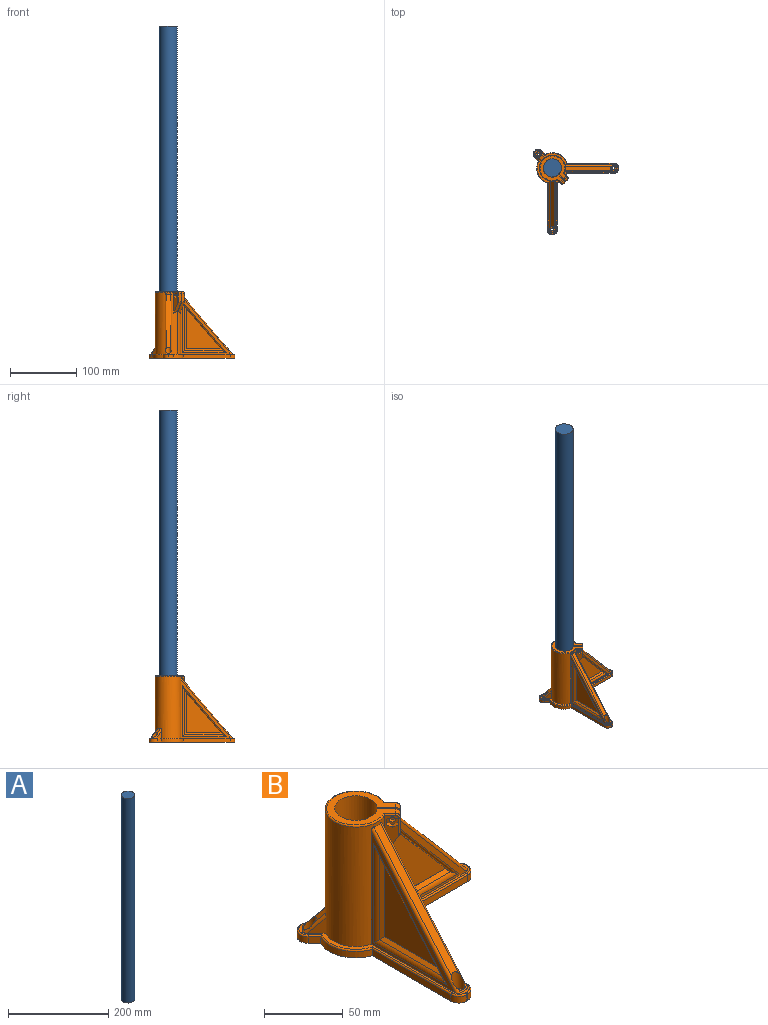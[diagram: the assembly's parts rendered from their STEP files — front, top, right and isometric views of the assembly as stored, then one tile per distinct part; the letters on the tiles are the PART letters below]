
ASSEMBLY  parts=2 mates=1
PART A: 3 faces, bbox 27x27x500 mm
  f0: cylinder r=13.5mm len=500mm, axis (0,0,-1), area 42411.5mm2, adj f1,f2
  f1: plane 27x27mm, normal (0,0,1), area 572.6mm2, adj f0
  f2: plane 27x27mm, normal (0,0,-1), area 572.6mm2, adj f0
PART B: 132 faces, bbox 129.9x129.9x100.3 mm
  f0: plane 5.4x5.4mm, normal (-0.5,0.5,0.71), area 6.3mm2, adj f9,f53,f122,f123
  f1: plane 6x2.19mm, normal (0.76,0,0.65), area 9.1mm2, adj f9,f56,f81,f82
  f2: plane 6x2.19mm, normal (0,-0.76,0.65), area 9.1mm2, adj f9,f50,f79,f80
  f3: plane 87.84x75.23mm, normal (0,-1,0), area 745.8mm2, adj f8,f9,f82,f118,f126,f127
  f4: plane 87.84x75.23mm, normal (0,1,0), area 745.8mm2, adj f8,f9,f81,f119,f130,f131
  f5: plane 87.84x75.23mm, normal (-1,0,0), area 745.8mm2, adj f8,f9,f80,f121,f124,f125
  f6: plane 31.32x6.36mm, normal (-0.71,-0.71,0), area 162.2mm2, adj f8,f34,f41,f42,f43,f44,f45,f46
  f7: cylinder r=2.2mm len=5.23mm, axis (0.71,0.71,0), area 41.5mm2, adj f25,f47
  f8: cylinder r=19.5mm len=93mm, axis (0,0,-1), area 8919.4mm2, adj f3,f4,f5,f6,f9,f24,f25,f27
  f9: plane 126.76x126.76mm, normal (0,0,1), area 852.8mm2, adj f0,f1,f2,f3,f4,f5,f8,f21
  f10: plane 70.73x5mm, normal (1,0,0), area 353.6mm2, adj f11,f23,f74,f96
  f11: cylinder r=23.5mm len=14.77mm, axis (0,0,-1), area 108.2mm2, adj f10,f12,f23,f94
  f12: plane 70.73x5mm, normal (0,-1,0), area 353.6mm2, adj f11,f23,f75,f92
  f13: plane 5x1mm, normal (1,0,0), area 5mm2, adj f23,f75,f76,f93
  f14: plane 70.73x5mm, normal (0,1,0), area 353.6mm2, adj f15,f23,f76,f97
  f15: cylinder r=23.5mm len=32.72mm, axis (0,0,-1), area 200.5mm2, adj f14,f16,f23,f99
  f16: plane 5.66x5.66mm, normal (0.71,0.71,0), area 40mm2, adj f15,f23,f77,f101
  f17: plane 5x0.71mm, normal (-0.71,0.71,0), area 5mm2, adj f23,f77,f78,f105
  f18: plane 5.66x5.66mm, normal (-0.71,-0.71,0), area 40mm2, adj f19,f23,f78,f108
  f19: cylinder r=23.5mm len=32.72mm, axis (0,0,-1), area 200.5mm2, adj f18,f20,f23,f106
  f20: plane 70.73x5mm, normal (-1,0,0), area 353.6mm2, adj f19,f23,f73,f104
  f21: cylinder r=13.5mm len=100mm, axis (0,0,-1), area 8341.2mm2, adj f9,f23,f24,f25,f26
  f22: plane 5x1mm, normal (0,-1,0), area 5mm2, adj f23,f73,f74,f100
  f23: plane 128.76x128.76mm, normal (0,0,-1), area 3573.5mm2, adj f10,f11,f12,f13,f14,f15,f16,f17
  f24: plane 94x10.48mm, normal (-0.71,-0.71,0), area 746.8mm2, adj f8,f9,f21,f26,f35,f37,f38,f109
  f25: plane 94x10.48mm, normal (0.71,0.71,0), area 746.8mm2, adj f7,f8,f9,f21,f26,f33,f34,f110
  f26: plane 40.45x40.45mm, normal (0,0,1), area 566.6mm2, adj f21,f24,f25,f109,f110,f113,f114,f115
  f27: plane 81.62x69.9mm, normal (0.76,0,0.65), area 635.1mm2, adj f8,f56,f81,f82
  f28: plane 87.84x75.23mm, normal (1,0,0), area 745.8mm2, adj f8,f9,f79,f120,f128,f129
  f29: plane 81.62x69.9mm, normal (0,-0.76,0.65), area 635.1mm2, adj f8,f50,f79,f80
  f30: plane 12.06x8.53mm, normal (0.71,0.71,0), area 72.7mm2, adj f8,f9,f123
  f31: plane 12.06x8.53mm, normal (-0.71,-0.71,0), area 72.7mm2, adj f8,f9,f122
  f32: plane 9.31x9.31mm, normal (-0.5,0.5,0.71), area 52mm2, adj f8,f53,f122,f123
  f33: plane 12x3.54mm, normal (0.71,-0.71,0), area 60mm2, adj f25,f34,f110,f117
  f34: plane 17.32x11.31mm, normal (0.61,-0.61,-0.5), area 110.5mm2, adj f6,f8,f25,f33,f117
  f35: plane 12x3.54mm, normal (0.71,-0.71,0), area 60mm2, adj f24,f37,f109,f111
  f36: plane 31.32x6.36mm, normal (0.71,0.71,0), area 157.6mm2, adj f8,f37,f40,f111,f112,f113
  f37: plane 17.32x11.31mm, normal (0.61,-0.61,-0.5), area 110.5mm2, adj f8,f24,f35,f36,f111
  f38: cylinder r=2.2mm len=4.53mm, axis (0.71,0.71,0), area 27.6mm2, adj f24,f39
  f39: plane 8.25x5.83mm, normal (0.71,0.71,0), area 38.3mm2, adj f38,f40
  f40: cylinder r=4.12mm len=8.66mm, axis (0.71,0.71,0), area 103.7mm2, adj f36,f39,f111
  f41: plane 4.33x2.12mm, normal (-0.71,0.71,0), area 13mm2, adj f6,f42,f46,f47
  f42: plane 4.77x4.77mm, normal (-0.35,0.35,-0.87), area 13mm2, adj f6,f41,f43,f47
  f43: plane 4.77x4.77mm, normal (0.35,-0.35,-0.87), area 13mm2, adj f6,f42,f44,f47
  f44: plane 4.33x2.12mm, normal (0.71,-0.71,0), area 13mm2, adj f6,f43,f45,f47
  f45: plane 4.77x4.77mm, normal (0.35,-0.35,0.87), area 13mm2, adj f6,f44,f46,f47
  f46: plane 4.77x4.77mm, normal (-0.35,0.35,0.87), area 13mm2, adj f6,f41,f45,f47
  f47: plane 8.66x5.3mm, normal (-0.71,-0.71,0), area 33.5mm2, adj f7,f41,f42,f43,f44,f45,f46
  f48: cylinder r=2.2mm len=4.4mm, axis (0,0,1), area 37.1mm2, adj f23,f49
  f49: plane 8.25x8.25mm, normal (0,0,1), area 38.3mm2, adj f48,f50
  f50: cylinder r=4.12mm len=13.64mm, axis (0,0,1), area 225.1mm2, adj f2,f29,f49,f79,f80
  f51: cylinder r=2.2mm len=4.4mm, axis (0,0,1), area 32.3mm2, adj f23,f52
  f52: plane 8.25x8.25mm, normal (0,0,1), area 38.3mm2, adj f51,f53
  f53: cylinder r=4.12mm len=12.25mm, axis (0,0,1), area 207.4mm2, adj f0,f32,f52,f122,f123
  f54: cylinder r=2.2mm len=4.4mm, axis (0,0,1), area 37.1mm2, adj f23,f55
  f55: plane 8.25x8.25mm, normal (0,0,1), area 38.3mm2, adj f54,f56
  f56: cylinder r=4.12mm len=13.64mm, axis (0,0,1), area 225.1mm2, adj f1,f27,f55,f81,f82
  f57: plane 61.28x0.1mm, normal (0,-1,0), area 6.1mm2, adj f58,f59,f60,f89
  f58: plane 52.48x0.1mm, normal (0,0,1), area 5.2mm2, adj f57,f59,f60,f90
  f59: plane 65.4x56mm, normal (0,0.76,-0.65), area 166.5mm2, adj f57,f58,f60,f89,f90,f121
  f60: plane 61.28x52.48mm, normal (-1,0,0), area 1607.8mm2, adj f57,f58,f59
  f61: plane 61.28x0.1mm, normal (0,-1,0), area 6.1mm2, adj f62,f63,f64,f85
  f62: plane 65.4x56mm, normal (0,0.76,-0.65), area 166.5mm2, adj f61,f63,f64,f85,f86,f120
  f63: plane 52.48x0.1mm, normal (0,0,1), area 5.2mm2, adj f61,f62,f64,f86
  f64: plane 61.28x52.48mm, normal (1,0,0), area 1607.8mm2, adj f61,f62,f63
  f65: plane 52.48x0.1mm, normal (0,0,1), area 5.2mm2, adj f66,f67,f68,f84
  f66: plane 61.28x0.1mm, normal (1,0,0), area 6.1mm2, adj f65,f67,f68,f83
  f67: plane 65.4x56mm, normal (-0.76,0,-0.65), area 166.5mm2, adj f65,f66,f68,f83,f84,f119
  f68: plane 61.28x52.48mm, normal (0,1,0), area 1607.8mm2, adj f65,f66,f67
  f69: plane 61.28x0.1mm, normal (1,0,0), area 6.1mm2, adj f70,f71,f72,f88
  f70: plane 52.48x0.1mm, normal (0,0,1), area 5.2mm2, adj f69,f71,f72,f87
  f71: plane 65.4x56mm, normal (-0.76,0,-0.65), area 166.5mm2, adj f69,f70,f72,f87,f88,f118
  f72: plane 61.28x52.48mm, normal (0,-1,0), area 1607.8mm2, adj f69,f70,f71
  f73: cylinder r=7mm len=7mm, axis (0,0,-1), area 55mm2, adj f20,f22,f23,f102
  f74: cylinder r=7mm len=7mm, axis (0,0,-1), area 55mm2, adj f10,f22,f23,f98
  f75: cylinder r=7mm len=7mm, axis (0,0,-1), area 55mm2, adj f12,f13,f23,f91
  f76: cylinder r=7mm len=7mm, axis (0,0,-1), area 55mm2, adj f13,f14,f23,f95
  f77: cylinder r=7mm len=9.9mm, axis (0,0,-1), area 55mm2, adj f16,f17,f23,f103
  f78: cylinder r=7mm len=9.9mm, axis (0,0,-1), area 55mm2, adj f17,f18,f23,f107
  f79: cylinder r=2mm len=91.77mm, axis (0,-0.65,-0.76), area 363.6mm2, adj f2,f8,f9,f28,f29,f50
  f80: cylinder r=2mm len=91.77mm, axis (0,0.65,0.76), area 363.6mm2, adj f2,f5,f8,f9,f29,f50
  f81: cylinder r=2mm len=91.77mm, axis (0.65,0,-0.76), area 363.6mm2, adj f1,f4,f8,f9,f27,f56
  f82: cylinder r=2mm len=91.77mm, axis (-0.65,0,0.76), area 363.6mm2, adj f1,f3,f8,f9,f27,f56
  f83: plane 66.7x2.47mm, normal (0.71,0.71,0), area 220.2mm2, adj f66,f67,f84,f119,f130
  f84: plane 57.12x2.46mm, normal (0,0.71,0.71), area 188.6mm2, adj f65,f67,f83,f119,f131
  f85: plane 66.7x2.47mm, normal (0.71,-0.71,0), area 220.2mm2, adj f61,f62,f86,f120,f128
  f86: plane 57.12x2.46mm, normal (0.71,0,0.71), area 188.6mm2, adj f62,f63,f85,f120,f129
  f87: plane 57.12x2.46mm, normal (0,-0.71,0.71), area 188.6mm2, adj f70,f71,f88,f118,f126
  f88: plane 66.7x2.47mm, normal (0.71,-0.71,0), area 220.2mm2, adj f69,f71,f87,f118,f127
  f89: plane 66.7x2.47mm, normal (-0.71,-0.71,0), area 220.2mm2, adj f57,f59,f90,f121,f124
  f90: plane 57.12x2.46mm, normal (-0.71,0,0.71), area 188.6mm2, adj f58,f59,f89,f121,f125
  f91: torus R=6mm, axis (0,0,1), area 16.4mm2, adj f9,f75,f92,f93
  f92: cylinder r=1mm len=71.46mm, axis (-1,0,0), area 111.5mm2, adj f9,f12,f91,f94
  f93: cylinder r=1mm len=1mm, axis (0,-1,0), area 1.6mm2, adj f9,f13,f91,f95
  f94: torus R=22.5mm, axis (0,0,1), area 34.3mm2, adj f9,f11,f92,f96
  f95: torus R=6mm, axis (0,0,1), area 16.4mm2, adj f9,f76,f93,f97
  f96: cylinder r=1mm len=71.46mm, axis (0,-1,0), area 111.5mm2, adj f9,f10,f94,f98
  f97: cylinder r=1mm len=71.46mm, axis (1,0,0), area 111.5mm2, adj f9,f14,f95,f99
  f98: torus R=6mm, axis (0,0,1), area 16.4mm2, adj f9,f74,f96,f100
  f99: torus R=22.5mm, axis (0,0,1), area 62.8mm2, adj f9,f15,f97,f101
  f100: cylinder r=1mm len=1mm, axis (-1,0,0), area 1.6mm2, adj f9,f22,f98,f102
  f101: cylinder r=1mm len=6.88mm, axis (0.71,-0.71,0), area 13mm2, adj f9,f16,f99,f103
  f102: torus R=6mm, axis (0,0,1), area 16.4mm2, adj f9,f73,f100,f104
  f103: torus R=6mm, axis (0,0,1), area 16.4mm2, adj f9,f77,f101,f105
  f104: cylinder r=1mm len=71.46mm, axis (0,1,0), area 111.5mm2, adj f9,f20,f102,f106
  f105: cylinder r=1mm len=1.41mm, axis (0.71,0.71,0), area 1.6mm2, adj f9,f17,f103,f107
  f106: torus R=22.5mm, axis (0,0,1), area 62.8mm2, adj f9,f19,f104,f108
  f107: torus R=6mm, axis (0,0,1), area 16.4mm2, adj f9,f78,f105,f108
  f108: cylinder r=1mm len=6.88mm, axis (-0.71,0.71,0), area 13mm2, adj f9,f18,f106,f107
  f109: cylinder r=3mm len=5.66mm, axis (0.71,0.71,0), area 23.6mm2, adj f24,f26,f35,f112
  f110: cylinder r=3mm len=5.66mm, axis (0.71,0.71,0), area 23.6mm2, adj f25,f26,f33,f116
  f111: cylinder r=1mm len=13.73mm, axis (0,0,1), area 19.7mm2, adj f35,f36,f37,f40,f112
  f112: torus R=2mm, axis (0.71,0.71,0), area 6.5mm2, adj f36,f109,f111,f113
  f113: cylinder r=1mm len=6.16mm, axis (-0.71,0.71,0), area 11.4mm2, adj f26,f36,f112,f114
  f114: torus R=18.5mm, axis (0,0,1), area 168.4mm2, adj f8,f26,f113,f115
  f115: cylinder r=1mm len=6.16mm, axis (0.71,-0.71,0), area 11.4mm2, adj f6,f26,f114,f116
  f116: torus R=2mm, axis (0.71,0.71,0), area 6.5mm2, adj f6,f110,f115,f117
  f117: cylinder r=1mm len=13.73mm, axis (0,0,1), area 19.8mm2, adj f6,f33,f34,f116
  f118: cylinder r=2mm len=78.6mm, axis (-0.65,0,0.76), area 291.6mm2, adj f3,f71,f87,f88,f126,f127
  f119: cylinder r=2mm len=78.6mm, axis (-0.65,0,0.76), area 291.6mm2, adj f4,f67,f83,f84,f130,f131
  f120: cylinder r=2mm len=78.6mm, axis (0,0.65,0.76), area 291.6mm2, adj f28,f62,f85,f86,f128,f129
  f121: cylinder r=2mm len=78.6mm, axis (0,0.65,0.76), area 291.6mm2, adj f5,f59,f89,f90,f124,f125
  f122: cylinder r=2mm len=15.92mm, axis (-0.5,0.5,-0.71), area 54.4mm2, adj f0,f8,f9,f31,f32,f53
  f123: cylinder r=2mm len=15.92mm, axis (0.5,-0.5,0.71), area 54.4mm2, adj f0,f8,f9,f30,f32,f53
  f124: cylinder r=5mm len=77.3mm, axis (0,0,-1), area 281mm2, adj f5,f89,f121,f125
  f125: cylinder r=5mm len=66.19mm, axis (0,1,0), area 240.6mm2, adj f5,f90,f121,f124
  f126: cylinder r=5mm len=66.19mm, axis (-1,0,0), area 240.6mm2, adj f3,f87,f118,f127
  f127: cylinder r=5mm len=77.3mm, axis (0,0,-1), area 281mm2, adj f3,f88,f118,f126
  f128: cylinder r=5mm len=77.3mm, axis (0,0,-1), area 281mm2, adj f28,f85,f120,f129
  f129: cylinder r=5mm len=66.19mm, axis (0,1,0), area 240.6mm2, adj f28,f86,f120,f128
  f130: cylinder r=5mm len=77.3mm, axis (0,0,-1), area 281mm2, adj f4,f83,f119,f131
  f131: cylinder r=5mm len=66.19mm, axis (-1,0,0), area 240.6mm2, adj f4,f84,f119,f130
PLACE A t=(-688.06,-208.42,186.02)mm
PLACE B t=(-646.58,-249.29,186.02)mm
MATE fastened A.f0 <-> B.f8  axis (0,0,-1) through (-646.58,-249.29,186.02)mm
